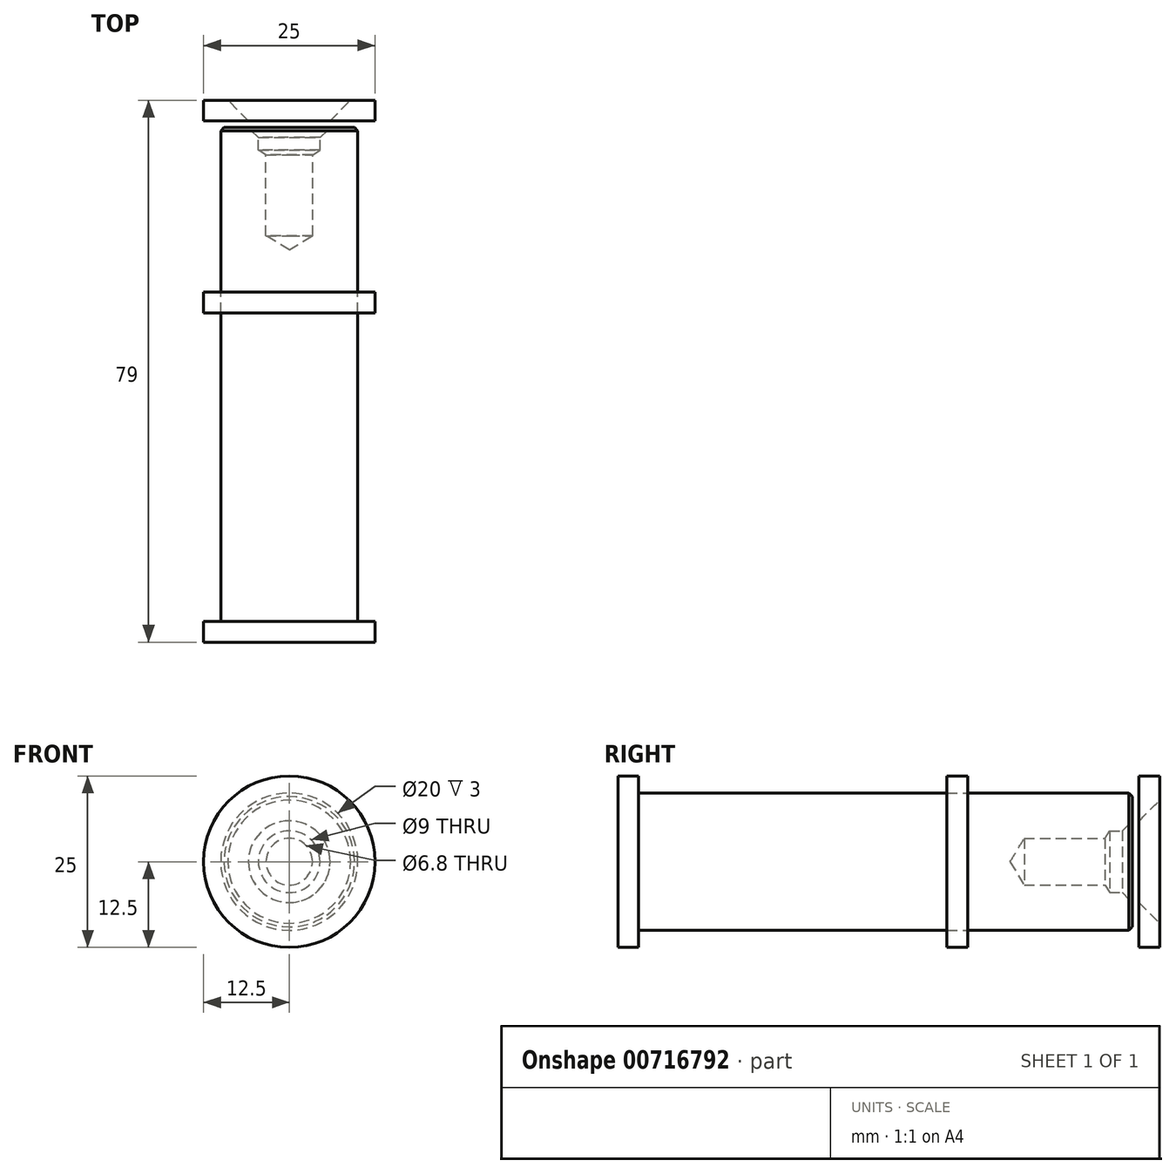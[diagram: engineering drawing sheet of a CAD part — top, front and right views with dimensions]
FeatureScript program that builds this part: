
annotation { "Feature Type Name" : "Feature", "Feature Type Description" : "" }
export const myFeature = defineFeature(function(context is Context, id is Id, definition is map)
    precondition{}
    {
        {
            var Q0;
            Q0=qCreatedBy(makeId("Right.planeOp"),FACE);
            var sketch = newSketch(context, id + "F0", { "sketchPlane" : qUnion([Q0])});
            skLineSegment(sketch, "E0", {"start": v(-37.5, 0) * mm, "end": v(37.5, 0) * mm});
            skLineSegment(sketch, "E1", {"start": v(37.5, 0) * mm, "end": v(37.5, 10) * mm});
            skLineSegment(sketch, "E2", {"start": v(37.5, 10) * mm, "end": v(-34.5, 10) * mm});
            skLineSegment(sketch, "E3", {"start": v(-34.5, 10) * mm, "end": v(-34.5, 12.5) * mm});
            skLineSegment(sketch, "E4", {"start": v(-34.5, 12.5) * mm, "end": v(-37.5, 12.5) * mm});
            skLineSegment(sketch, "E5", {"start": v(-37.5, 12.5) * mm, "end": v(-37.5, 0) * mm});
            skSolve(sketch);
        }
        {
            var Q0;
            Q0 = qSketchRegion(id + "F0", true);
            var Q1;
            Q1=sQuery(id+"F0.wireOp",EDGE,"E0");
            revolve(context, id + "F1", {"surfaceOperationType" : NewSurfaceOperationType.NEW, "entities" : qUnion([Q0]), "axis" : qUnion([Q1]), "revolveType" : RevolveType.FULL});
        }
        {
            var Q0;
            Q0=makeQuery(id+"F1.opRevolve","SWEPT_FACE",FACE,{"disambiguationData":[OSD([sQuery(id+"F0.wireOp",EDGE,"E1")])]});
            cPlane(context, id + "F2", {"entities" : qUnion([Q0]), "cplaneType" : CPlaneType.OFFSET, "offset" : 3 * mm, "width" : 150 * mm, "height" : 150 * mm});
        }
        {
            var Q0;
            Q0=qCreatedBy(id+"F2.planeOp",FACE);
            var sketch = newSketch(context, id + "F3", { "sketchPlane" : qUnion([Q0])});
            skPoint(sketch, "E6", {"position": v(0, 0) * mm});
            skSolve(sketch);
        }
        {
            var Q0;
            Q0=sQuery(id+"F3.wireOp",VERTEX,"E6");
            var Q1;
            Q1=makeQuery(id+"F1.opRevolve","SWEPT_BODY",BODY,{"disambiguationData":[OSD([sQuery(id+"F0.wireOp",EDGE,"E0"),sQuery(id+"F0.wireOp",EDGE,"E1"),sQuery(id+"F0.wireOp",EDGE,"E2"),sQuery(id+"F0.wireOp",EDGE,"E3"),sQuery(id+"F0.wireOp",EDGE,"E4"),sQuery(id+"F0.wireOp",EDGE,"E5")])]});
            hole(context, id + "F4", {"style" : HoleStyle.C_SINK, "endStyle" : HoleEndStyle.BLIND, "holeDiameter" : 9 * mm, "cSinkDiameter" : 17.92 * mm, "cSinkAngle" : 90 * degree, "majorDiameter" : 5 * mm, "holeDepth" : 6.3 * mm, "isTappedThrough" : true, "tappedDepth" : 12 * mm, "tapClearance" : 3, "startFromSketch" : true, "locations" : qUnion([Q0]), "scope" : qUnion([Q1])});
        }
        {
            var Q0;
            Q0=makeQuery(id+"F1.opRevolve","SWEPT_FACE",FACE,{"disambiguationData":[OSD([sQuery(id+"F0.wireOp",EDGE,"E1")])]});
            var sketch = newSketch(context, id + "F5", { "sketchPlane" : qUnion([Q0])});
            skPoint(sketch, "E7", {"position": v(0, 0) * mm});
            skSolve(sketch);
        }
        {
            var Q0;
            Q0=sQuery(id+"F5.wireOp",VERTEX,"E7");
            var Q1;
            Q1=makeQuery(id+"F1.opRevolve","SWEPT_BODY",BODY,{"disambiguationData":[OSD([sQuery(id+"F0.wireOp",EDGE,"E0"),sQuery(id+"F0.wireOp",EDGE,"E1"),sQuery(id+"F0.wireOp",EDGE,"E2"),sQuery(id+"F0.wireOp",EDGE,"E3"),sQuery(id+"F0.wireOp",EDGE,"E4"),sQuery(id+"F0.wireOp",EDGE,"E5")])]});
            hole(context, id + "F6", {"style" : HoleStyle.SIMPLE, "endStyle" : HoleEndStyle.BLIND, "standardTappedOrClearance" : lookupTablePath({ "standard" : "ISO", "engagement" : "75%", "pitch" : "1.25 mm", "size" : "M8", "type" : "Tapped" }), "standardBlindInLast" : lookupTablePath({ "standard" : "ISO", "engagement" : "75%", "pitch" : "1.25 mm", "size" : "M8", "type" : "Tapped" }), "holeDiameter" : 6.8 * mm, "majorDiameter" : 8 * mm, "showTappedDepth" : true, "holeDepth" : 15.75 * mm, "isTappedThrough" : true, "tappedDepth" : 12 * mm, "tapClearance" : 3, "startFromSketch" : true, "locations" : qUnion([Q0]), "scope" : qUnion([Q1])});
        }
        {
            var Q0;
            Q0=makeQuery(id+"F1.opRevolve","SWEPT_FACE",FACE,{"disambiguationData":[OSD([sQuery(id+"F0.wireOp",EDGE,"E1")])]});
            cPlane(context, id + "F7", {"entities" : qUnion([Q0]), "cplaneType" : CPlaneType.OFFSET, "offset" : 1 * mm, "width" : 150 * mm, "height" : 150 * mm});
        }
        {
            var Q0;
            Q0=qCreatedBy(id+"F7.planeOp",FACE);
            var sketch = newSketch(context, id + "F8", { "sketchPlane" : qUnion([Q0])});
            skCircle(sketch, "E8", {"center": v(0, 0) * mm, "radius": 12.5 * mm});
            skSolve(sketch);
        }
        {
            var Q0;
            Q0=makeQuery(id+"F8.imprint","IMPRINT",FACE,{"disambiguationData":[TD([[makeQuery(id+"F8.imprint","IMPRINT",EDGE,{"derivedFrom":sQuery(id+"F8.wireOp",EDGE,"E8")}),1.0]])]});
            var Q1;
            {var subQ0=sQuery(id+"F0.wireOp",EDGE,"E1");Q1=makeQuery(id+"F8.imprint","IMPRINT",FACE,{"disambiguationData":[TD([[makeQuery(id+"F8.imprint","IMPRINT",EDGE,{"derivedFrom":makeQuery(id+"F1.opRevolve","SWEPT_EDGE",EDGE,{"disambiguationData":[OSD([subQ0,sQuery(id+"F0.wireOp",EDGE,"E2")])]})}),-1.0]])]});}
            var Q2;
            Q2=makeQuery(id+"F8.imprint","IMPRINT",FACE,{"disambiguationData":[TD([[makeQuery(id+"F8.imprint","IMPRINT",EDGE,{"derivedFrom":makeQuery(id+"F4.hole-0.boolean.opBoolean","INTERSECT",EDGE,{"derivedFrom":[makeQuery(id+"F1.opRevolve","SWEPT_FACE",FACE,{"disambiguationData":[OSD([sQuery(id+"F0.wireOp",EDGE,"E1")])]}),makeQuery(id+"F4.hole-0.opRevolve","SWEPT_FACE",FACE,{"disambiguationData":[OSD([sQuery(id+"F4.hole-0.sketch.wireOp",EDGE,"csink_start_line_1")])]})]})}),1.0]])]});
            extrude(context, id + "F9", {"entities" : qUnion([Q0, Q1, Q2]), "depth" : 3 * mm, "offsetDistance" : 25 * mm});
        }
        {
            var Q0;
            Q0=makeQuery(id+"F9.opExtrude","CAP_FACE",FACE,{"disambiguationData":[OSD([sQuery(id+"F8.wireOp",EDGE,"E8")])],"isStart":false});
            var sketch = newSketch(context, id + "F10", { "sketchPlane" : qUnion([Q0])});
            skPoint(sketch, "E9", {"position": v(0, 0) * mm});
            skSolve(sketch);
        }
        {
            var Q0;
            Q0=sQuery(id+"F10.wireOp",VERTEX,"E9");
            var Q1;
            Q1=makeQuery(id+"F9.opExtrude","SWEPT_BODY",BODY,{"disambiguationData":[OSD([sQuery(id+"F8.wireOp",EDGE,"E8")])]});
            hole(context, id + "F11", {"style" : HoleStyle.C_SINK, "endStyle" : HoleEndStyle.BLIND, "standardTappedOrClearance" : lookupTablePath({ "standard" : "ISO", "engagement" : "75%", "pitch" : "1.25 mm", "size" : "M8", "type" : "Tapped" }), "standardBlindInLast" : lookupTablePath({ "standard" : "ISO", "engagement" : "75%", "pitch" : "1.25 mm", "size" : "M8", "type" : "Tapped" }), "holeDiameter" : 6.8 * mm, "cSinkDiameter" : 17.92 * mm, "cSinkAngle" : 90 * degree, "majorDiameter" : 8 * mm, "showTappedDepth" : true, "holeDepth" : 15.75 * mm, "isTappedThrough" : true, "tappedDepth" : 12 * mm, "tapClearance" : 3, "startFromSketch" : true, "locations" : qUnion([Q0]), "scope" : qUnion([Q1])});
        }
        {
            var Q0;
            Q0=makeQuery(id+"F1.opRevolve","SWEPT_EDGE",EDGE,{"disambiguationData":[OSD([sQuery(id+"F0.wireOp",EDGE,"E1"),sQuery(id+"F0.wireOp",EDGE,"E2")])]});
            chamfer(context, id + "F12", {"entities" : qUnion([Q0]), "width" : 0.5 * mm, "tangentPropagation" : true});
        }
        {
            var Q0;
            Q0=makeQuery(id+"F9.opExtrude","CAP_FACE",FACE,{"disambiguationData":[OSD([sQuery(id+"F8.wireOp",EDGE,"E8")])],"isStart":true});
            cPlane(context, id + "F13", {"entities" : qUnion([Q0]), "cplaneType" : CPlaneType.OFFSET, "offset" : 25 * mm, "width" : 150 * mm, "height" : 150 * mm});
        }
        {
            var Q0;
            Q0=qCreatedBy(id+"F13.planeOp",FACE);
            var sketch = newSketch(context, id + "F14", { "sketchPlane" : qUnion([Q0])});
            skCircle(sketch, "E10", {"center": v(0, 0) * mm, "radius": 12.5 * mm});
            skCircle(sketch, "E11", {"center": v(0, 0) * mm, "radius": 10 * mm});
            skSolve(sketch);
        }
        {
            var Q0;
            Q0 = qSketchRegion(id + "F14", true);
            extrude(context, id + "F15", {"entities" : qUnion([Q0]), "depth" : 3 * mm, "offsetDistance" : 25 * mm});
        }
    });
